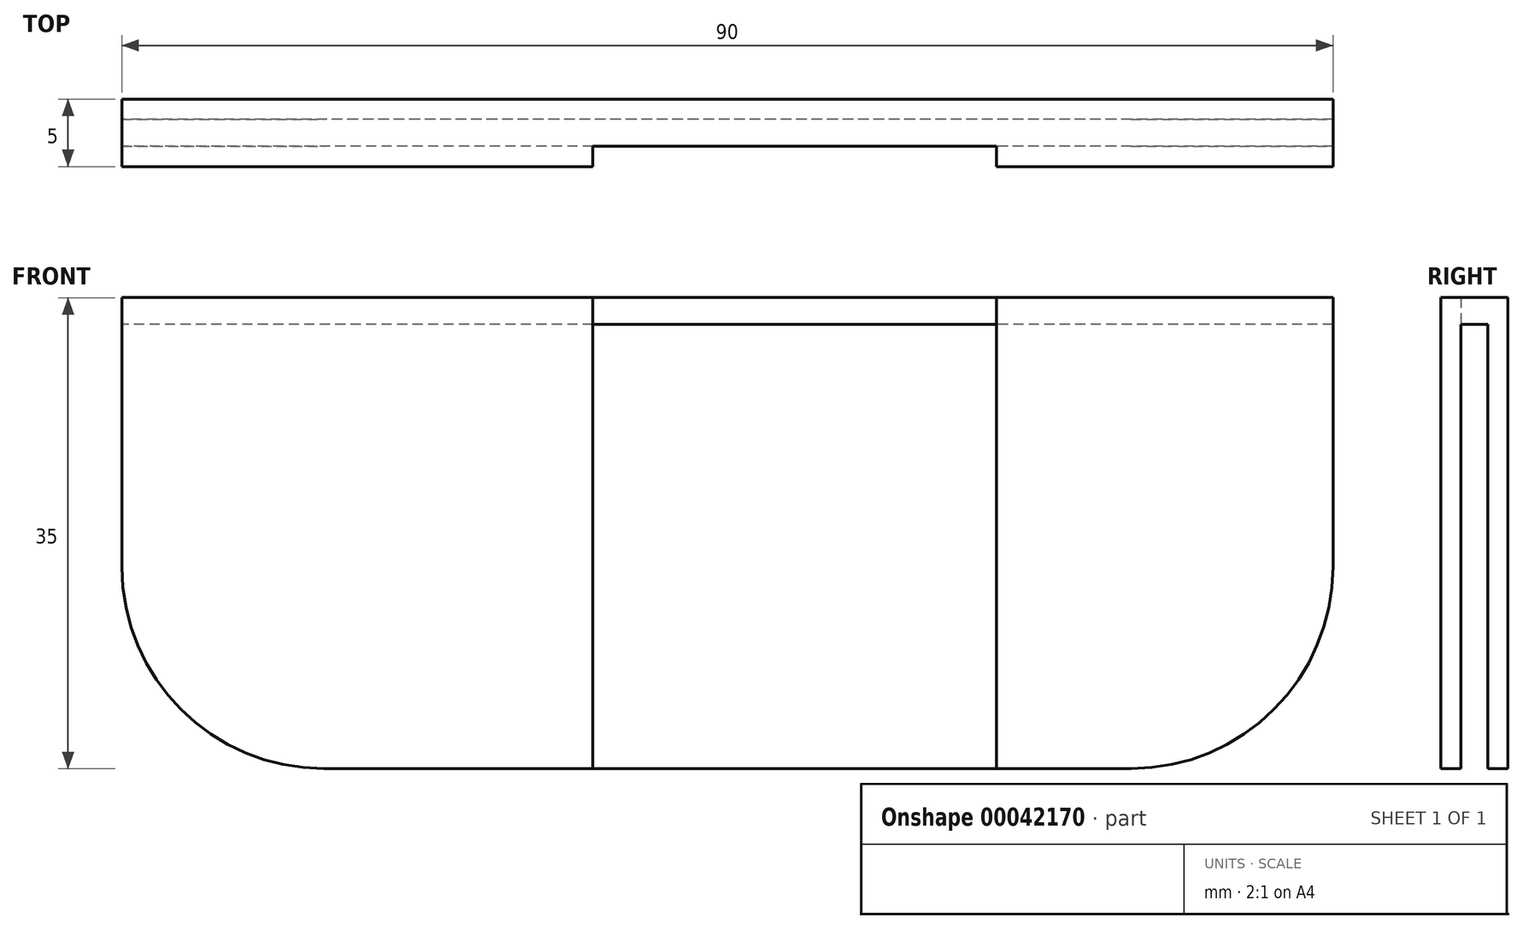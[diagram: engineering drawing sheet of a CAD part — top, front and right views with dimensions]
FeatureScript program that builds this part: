
annotation { "Feature Type Name" : "Feature", "Feature Type Description" : "" }
export const myFeature = defineFeature(function(context is Context, id is Id, definition is map)
    precondition{}
    {
        {
            var Q0;
            Q0=qCreatedBy(makeId("Front.planeOp"),FACE);
            var sketch = newSketch(context, id + "F0", { "sketchPlane" : qUnion([Q0])});
            skLineSegment(sketch, "E0.bottom", {"start": v(-47.33, 18.7) * mm, "end": v(42.67, 18.7) * mm});
            skLineSegment(sketch, "E0.top", {"start": v(-47.33, -16.3) * mm, "end": v(42.67, -16.3) * mm});
            skLineSegment(sketch, "E0.left", {"start": v(-47.33, 18.7) * mm, "end": v(-47.33, -16.3) * mm});
            skLineSegment(sketch, "E0.right", {"start": v(42.67, 18.7) * mm, "end": v(42.67, -16.3) * mm});
            skSolve(sketch);
        }
        {
            var Q0;
            Q0 = qSketchRegion(id + "F0", true);
            var Q1;
            Q1=makeQuery(id+"F0.imprint","IMPRINT",FACE,{"disambiguationData":[TD([[makeQuery(id+"F0.imprint","IMPRINT",EDGE,{"derivedFrom":sQuery(id+"F0.wireOp",EDGE,"E0.bottom")}),-1.0]])]});
            extrude(context, id + "F1", {"entities" : qUnion([Q0, Q1]), "depth" : 5 * mm});
        }
        {
            var Q0;
            Q0=makeQuery(id+"F1.opExtrude","SWEPT_FACE",FACE,{"disambiguationData":[OSD([sQuery(id+"F0.wireOp",EDGE,"E0.left")])]});
            var sketch = newSketch(context, id + "F2", { "sketchPlane" : qUnion([Q0])});
            skLineSegment(sketch, "E1.bottom", {"start": v(1.5, -16.3) * mm, "end": v(3.5, -16.3) * mm});
            skLineSegment(sketch, "E1.top", {"start": v(1.5, 16.7) * mm, "end": v(3.5, 16.7) * mm});
            skLineSegment(sketch, "E1.left", {"start": v(1.5, -16.3) * mm, "end": v(1.5, 16.7) * mm});
            skLineSegment(sketch, "E1.right", {"start": v(3.5, -16.3) * mm, "end": v(3.5, 16.7) * mm});
            skSolve(sketch);
        }
        {
            var Q0;
            {var subQ0=sQuery(id+"F0.wireOp",EDGE,"E0.top");var subQ1=sQuery(id+"F0.wireOp",EDGE,"E0.left");Q0=makeQuery(id+"F4.boolean.opBoolean","SPLIT",EDGE,{"disambiguationData":[TD([makeQuery(id+"F4.opExtrude","SWEPT_FACE",FACE,{"disambiguationData":[OSD([sQuery(id+"F2.wireOp",EDGE,"125a9588-9129-41ff-91c0-09fd35678c61.bottom")])]})])],"derivedFrom":makeQuery(id+"F1.opExtrude","SWEPT_EDGE",EDGE,{"disambiguationData":[OSD([subQ0,subQ1])]})});}
            var Q1;
            Q1=makeQuery(id+"F1.opExtrude","SWEPT_EDGE",EDGE,{"disambiguationData":[OSD([sQuery(id+"F0.wireOp",EDGE,"E0.top"),sQuery(id+"F0.wireOp",EDGE,"E0.right")])]});
            fillet(context, id + "F3", {"entities" : qUnion([Q0, Q1]), "radius" : 15 * mm, "tangentPropagation" : true, "allowEdgeOverflow" : false});
        }
        {
            var Q0;
            Q0=makeQuery(id+"F2.imprint","IMPRINT",FACE,{"disambiguationData":[TD([[makeQuery(id+"F2.imprint","IMPRINT",EDGE,{"derivedFrom":sQuery(id+"F2.wireOp",EDGE,"E1.bottom")}),-1.0]])]});
            extrude(context, id + "F4", {"entities" : qUnion([Q0]), "operationType" : NewBodyOperationType.REMOVE, "oppositeDirection" : true, "depth" : 90 * mm});
        }
        {
            var Q0;
            Q0=makeQuery(id+"F1.opExtrude","CAP_FACE",FACE,{"disambiguationData":[OSD([sQuery(id+"F0.wireOp",EDGE,"E0.bottom"),sQuery(id+"F0.wireOp",EDGE,"E0.top"),sQuery(id+"F0.wireOp",EDGE,"E0.left"),sQuery(id+"F0.wireOp",EDGE,"E0.right")])],"isStart":false});
            var sketch = newSketch(context, id + "F5", { "sketchPlane" : qUnion([Q0])});
            skLineSegment(sketch, "E2.bottom", {"start": v(-12.33, 18.7) * mm, "end": v(17.67, 18.7) * mm});
            skLineSegment(sketch, "E2.top", {"start": v(-12.33, -16.3) * mm, "end": v(17.67, -16.3) * mm});
            skLineSegment(sketch, "E2.left", {"start": v(-12.33, 18.7) * mm, "end": v(-12.33, -16.3) * mm});
            skLineSegment(sketch, "E2.right", {"start": v(17.67, 18.7) * mm, "end": v(17.67, -16.3) * mm});
            skSolve(sketch);
        }
        {
            var Q0;
            Q0=makeQuery(id+"F5.imprint","IMPRINT",FACE,{"disambiguationData":[TD([[makeQuery(id+"F5.imprint","IMPRINT",EDGE,{"derivedFrom":sQuery(id+"F5.wireOp",EDGE,"E2.bottom")}),-1.0]])]});
            extrude(context, id + "F6", {"entities" : qUnion([Q0]), "operationType" : NewBodyOperationType.REMOVE, "oppositeDirection" : true, "depth" : 1.5 * mm});
        }
    });
